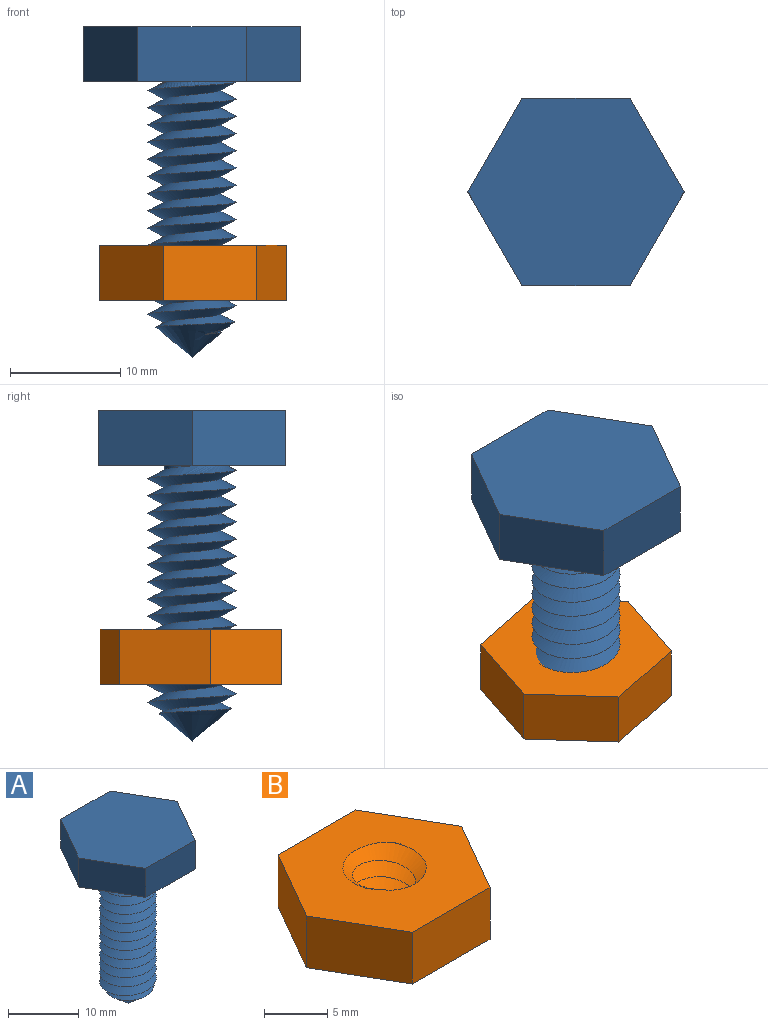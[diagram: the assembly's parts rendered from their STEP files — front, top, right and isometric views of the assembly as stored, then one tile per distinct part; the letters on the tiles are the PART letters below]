
ASSEMBLY  parts=2 mates=1
PART A: 15 faces, bbox 20.8x18.2x31.2 mm
  f0: bspline ~24.48x9.24mm, area 493.1mm2, adj f1,f2,f12,f13,f14
  f1: bspline ~22.92x9.24mm, area 480.5mm2, adj f0,f11,f13,f14
  f2: plane 20.81x18.18mm, normal (0,0,-1), area 223.6mm2, adj f0,f3,f4,f5,f6,f7,f8,f9
  f3: cylinder r=2.5mm len=5mm, axis (0,0,1), area 3.1mm2, adj f2,f11,f12
  f4: plane 8.5x5mm, normal (0.87,-0.5,0), area 49.1mm2, adj f2,f5,f9,f10
  f5: plane 8.5x5mm, normal (0.87,0.5,0), area 49.1mm2, adj f2,f4,f6,f10
  f6: plane 9.82x5mm, normal (0,1,0), area 49.1mm2, adj f2,f5,f7,f10
  f7: plane 8.5x5mm, normal (-0.87,0.5,0), area 49.1mm2, adj f2,f6,f8,f10
  f8: plane 8.5x5mm, normal (-0.87,-0.5,0), area 49.1mm2, adj f2,f7,f9,f10
  f9: plane 9.82x5mm, normal (0,-1,0), area 49.1mm2, adj f2,f4,f8,f10
  f10: plane 19.63x17mm, normal (0,0,1), area 250.3mm2, adj f4,f5,f6,f7,f8,f9
  f11: plane 1.5x0.78mm, normal (0,1,0), area 0.6mm2, adj f1,f2,f3,f12
  f12: bspline ~5x2.89mm, area 0mm2, adj f0,f2,f3,f11
  f13: cone r=0mm half-angle=50.2deg, axis (0,0,1), area 42.9mm2, adj f0,f1,f14
  f14: cone r=0mm half-angle=50.2deg, axis (0,0,1), area 1mm2, adj f0,f1,f13
PART B: 10 faces, bbox 18.5x16.2x8 mm
  f0: bspline ~9.24x8mm, area 110.6mm2, adj f1,f2,f3
  f1: bspline ~9.24x8mm, area 110.6mm2, adj f0,f2,f3
  f2: plane 18.51x16.19mm, normal (0,0,-1), area 161.1mm2, adj f0,f1,f4,f5,f6,f7,f8,f9
  f3: plane 18.53x16.21mm, normal (0,0,1), area 161.1mm2, adj f0,f1,f4,f5,f6,f7,f8,f9
  f4: plane 8.66x5mm, normal (0,-1,0), area 43.3mm2, adj f2,f3,f5,f9
  f5: plane 7.5x5mm, normal (0.87,-0.5,0), area 43.3mm2, adj f2,f3,f4,f6
  f6: plane 7.5x5mm, normal (0.87,0.5,0), area 43.3mm2, adj f2,f3,f5,f7
  f7: plane 8.66x5mm, normal (0,1,0), area 43.3mm2, adj f2,f3,f6,f8
  f8: plane 7.5x5mm, normal (-0.87,0.5,0), area 43.3mm2, adj f2,f3,f7,f9
  f9: plane 7.5x5mm, normal (-0.87,-0.5,0), area 43.3mm2, adj f2,f3,f4,f8
PLACE A t=(-9.97,-11,2.14)mm fixed
PLACE B rot(axis=(0,0,1),11.8deg) t=(-9.89,-10.9,-24.58)mm
MATE cylindrical A.f3 <-> B.f3  axis (0,0,1) through (-9.97,-11,7.14)mm
